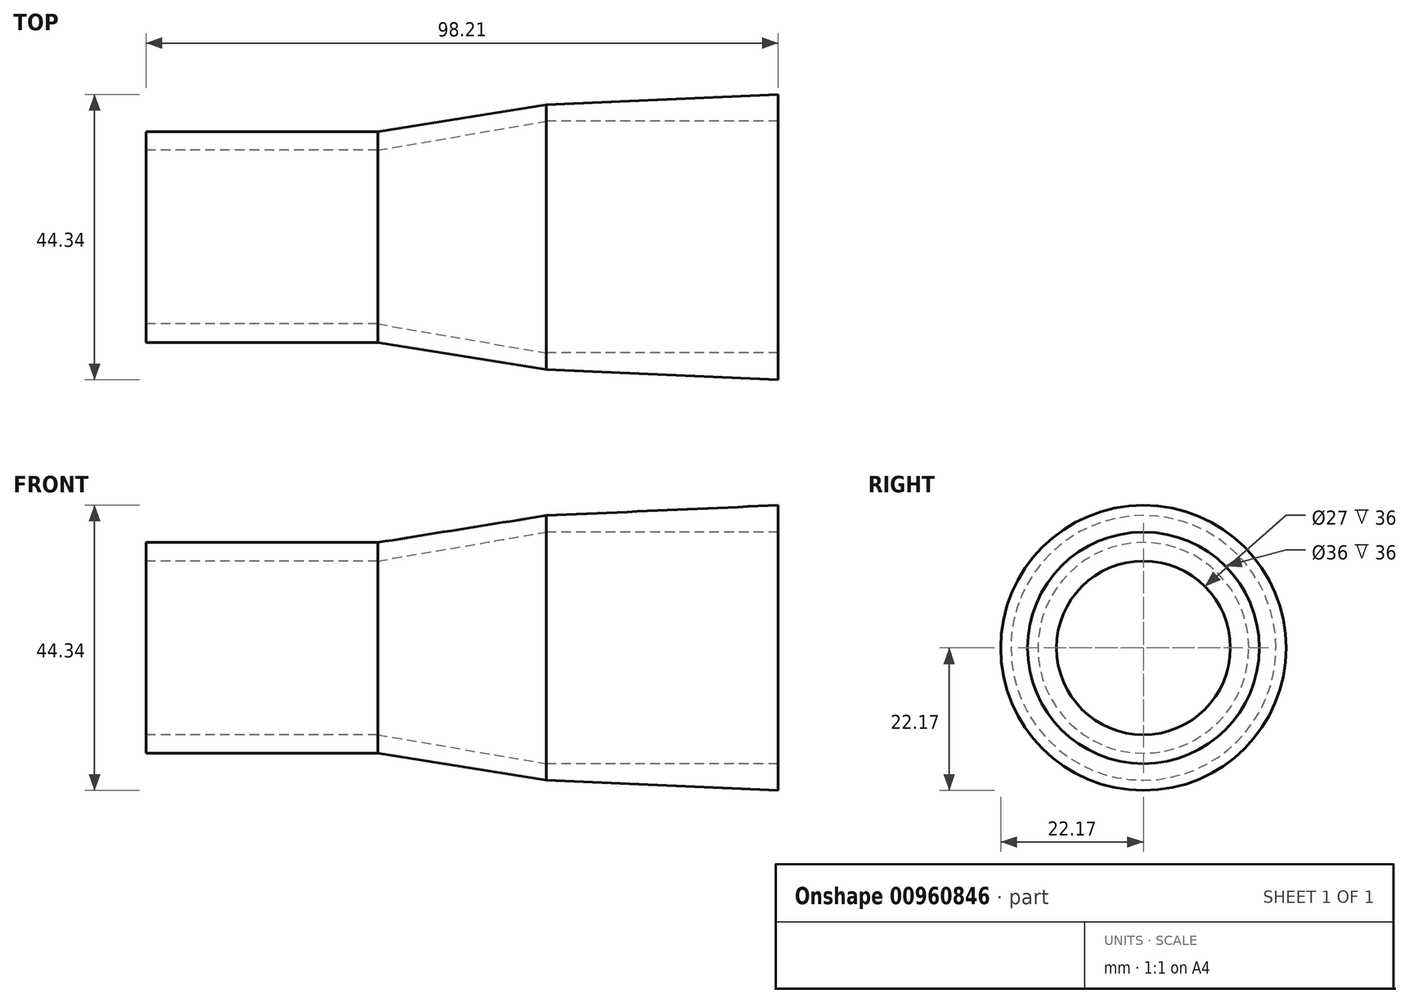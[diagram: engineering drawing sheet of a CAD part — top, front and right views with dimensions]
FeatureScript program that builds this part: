
annotation { "Feature Type Name" : "Feature", "Feature Type Description" : "" }
export const myFeature = defineFeature(function(context is Context, id is Id, definition is map)
    precondition{}
    {
        {
            var Q0;
            Q0=qCreatedBy(makeId("Top.planeOp"),FACE);
            var sketch = newSketch(context, id + "F0", { "sketchPlane" : qUnion([Q0])});
            skLineSegment(sketch, "E0", {"start": v(40.7, 22.24) * mm, "end": v(40.7, 18) * mm});
            skLineSegment(sketch, "E1", {"start": v(40.7, 18) * mm, "end": v(4.7, 18) * mm});
            skLineSegment(sketch, "E2", {"start": v(4.7, 18) * mm, "end": v(-21.5, 13.5) * mm});
            skLineSegment(sketch, "E3", {"start": v(-21.5, 13.5) * mm, "end": v(-57.5, 13.5) * mm});
            skLineSegment(sketch, "E4", {"start": v(-57.5, 13.5) * mm, "end": v(-57.5, 16.38) * mm});
            skLineSegment(sketch, "E5", {"start": v(-57.5, 16.38) * mm, "end": v(-21.5, 16.38) * mm});
            skLineSegment(sketch, "E6", {"start": v(-21.5, 16.38) * mm, "end": v(4.7, 20.58) * mm});
            skLineSegment(sketch, "E7", {"start": v(4.7, 20.58) * mm, "end": v(42.43, 22.24) * mm});
            skLineSegment(sketch, "E8", {"start": v(-43.34, 0) * mm, "end": v(39.1, 0) * mm, "construction": true});
            skLineSegment(sketch, "E9", {"start": v(22.7, 18) * mm, "end": v(22.7, 0) * mm, "construction": true});
            skPoint(sketch, "E10", {"position": v(-31.2, 13.5) * mm});
            skLineSegment(sketch, "E11", {"start": v(-31.2, 13.5) * mm, "end": v(-31.2, 0) * mm, "construction": true});
            skSolve(sketch);
        }
        {
            var Q0;
            {var subQ0=sQuery(id+"F0.wireOp",EDGE,"E1");Q0=makeQuery(id+"F0.imprint","IMPRINT",FACE,{"disambiguationData":[TD([[makeQuery(id+"F0.imprint","IMPRINT",EDGE,{"derivedFrom":subQ0}),-1.0]])]});}
            var Q1;
            Q1=sQuery(id+"F0.wireOp",EDGE,"E8");
            revolve(context, id + "F1", {"surfaceOperationType" : NewSurfaceOperationType.NEW, "entities" : qUnion([Q0]), "axis" : qUnion([Q1]), "revolveType" : RevolveType.FULL});
        }
    });
